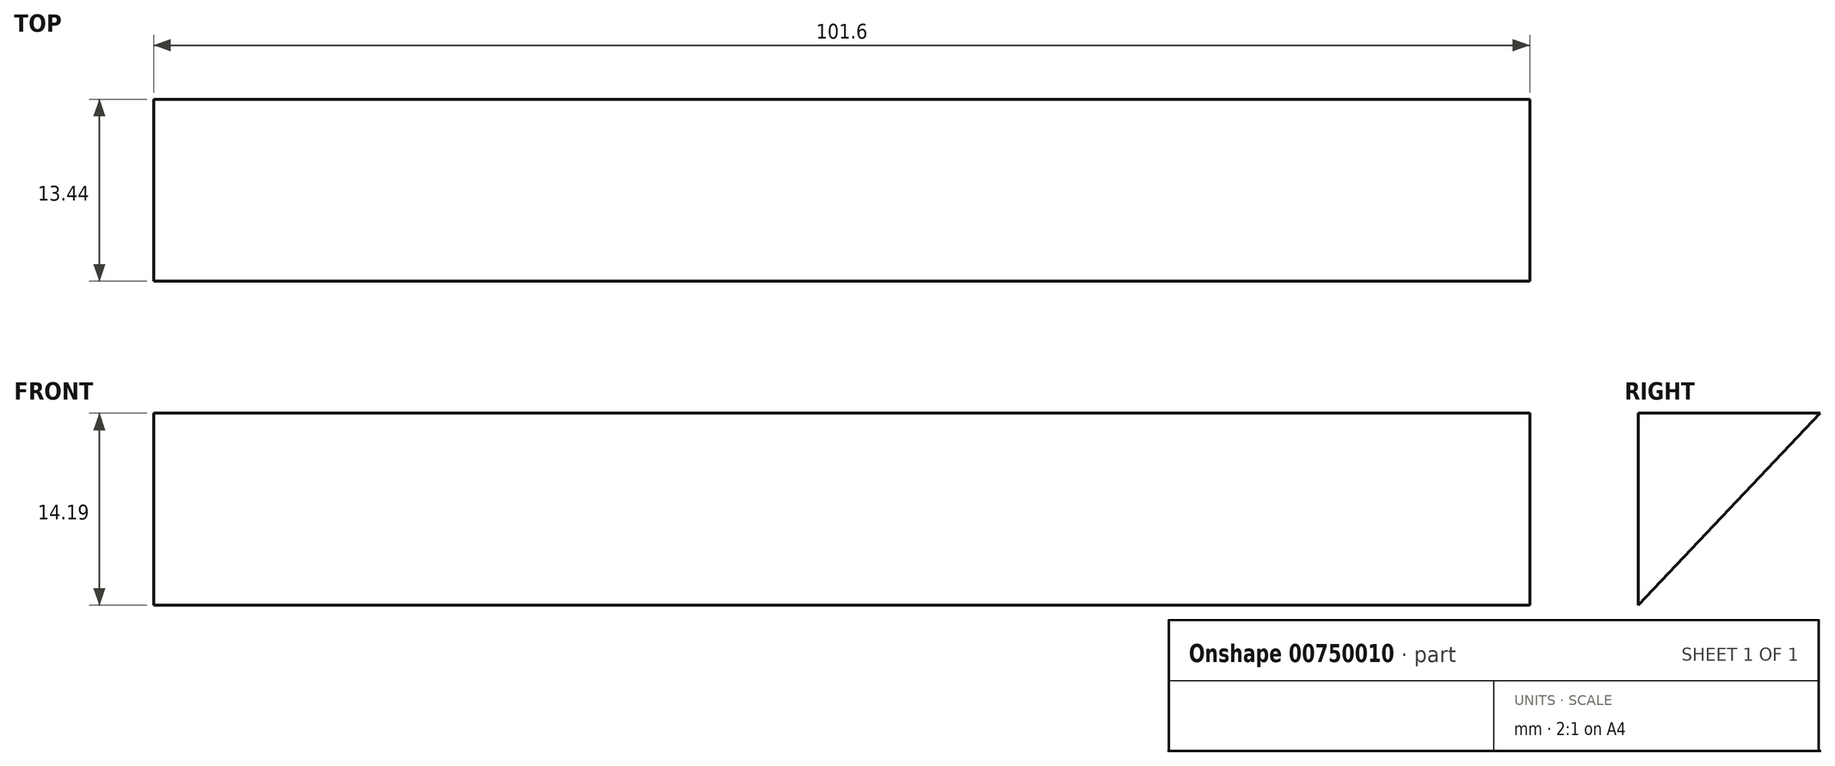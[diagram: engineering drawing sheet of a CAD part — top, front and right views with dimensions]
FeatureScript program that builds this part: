
annotation { "Feature Type Name" : "Feature", "Feature Type Description" : "" }
export const myFeature = defineFeature(function(context is Context, id is Id, definition is map)
    precondition{}
    {
        {
            var Q0;
            Q0=qCreatedBy(makeId("Right.planeOp"),FACE);
            var sketch = newSketch(context, id + "F0", { "sketchPlane" : qUnion([Q0])});
            skLineSegment(sketch, "E0.bottom", {"start": v(0, 0) * mm, "end": v(13.44, 0) * mm});
            skLineSegment(sketch, "E0.top", {"start": v(0, 14.2) * mm, "end": v(13.44, 14.2) * mm});
            skLineSegment(sketch, "E0.left", {"start": v(0, 0) * mm, "end": v(0, 14.2) * mm});
            skLineSegment(sketch, "E0.right", {"start": v(13.44, 0) * mm, "end": v(13.44, 14.2) * mm});
            skLineSegment(sketch, "E1", {"start": v(0, 0) * mm, "end": v(13.44, 14.2) * mm});
            skSolve(sketch);
        }
        {
            var Q0;
            Q0=makeQuery(id+"F0.imprint","IMPRINT",FACE,{"disambiguationData":[TD([[makeQuery(id+"F0.imprint","IMPRINT",EDGE,{"derivedFrom":sQuery(id+"F0.wireOp",EDGE,"E0.top")}),-1.0]])]});
            extrude(context, id + "F1", {"entities" : qUnion([Q0]), "depth" : 101.6 * mm, "offsetDistance" : 25.4 * mm});
        }
    });
